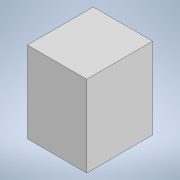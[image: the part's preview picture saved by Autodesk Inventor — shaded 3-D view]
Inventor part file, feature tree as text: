
AUTODESK INVENTOR PART (.ipt)
format: ipt  version: 2020.2 (Build 242310000, 310)  size: 86,528 bytes
history: native  units: mm
features: extrude x1, sketch x1
ambient origin geometry x8: Origin, YZ Plane, XZ Plane, XY Plane, X Axis, Y Axis, Z Axis, Center Point
bodies: Solide1 (feature_tree)
feature tree (2):
  extrude  "Extrusion1"  Depth=27.0mm
  sketch  "Esquisse1"
